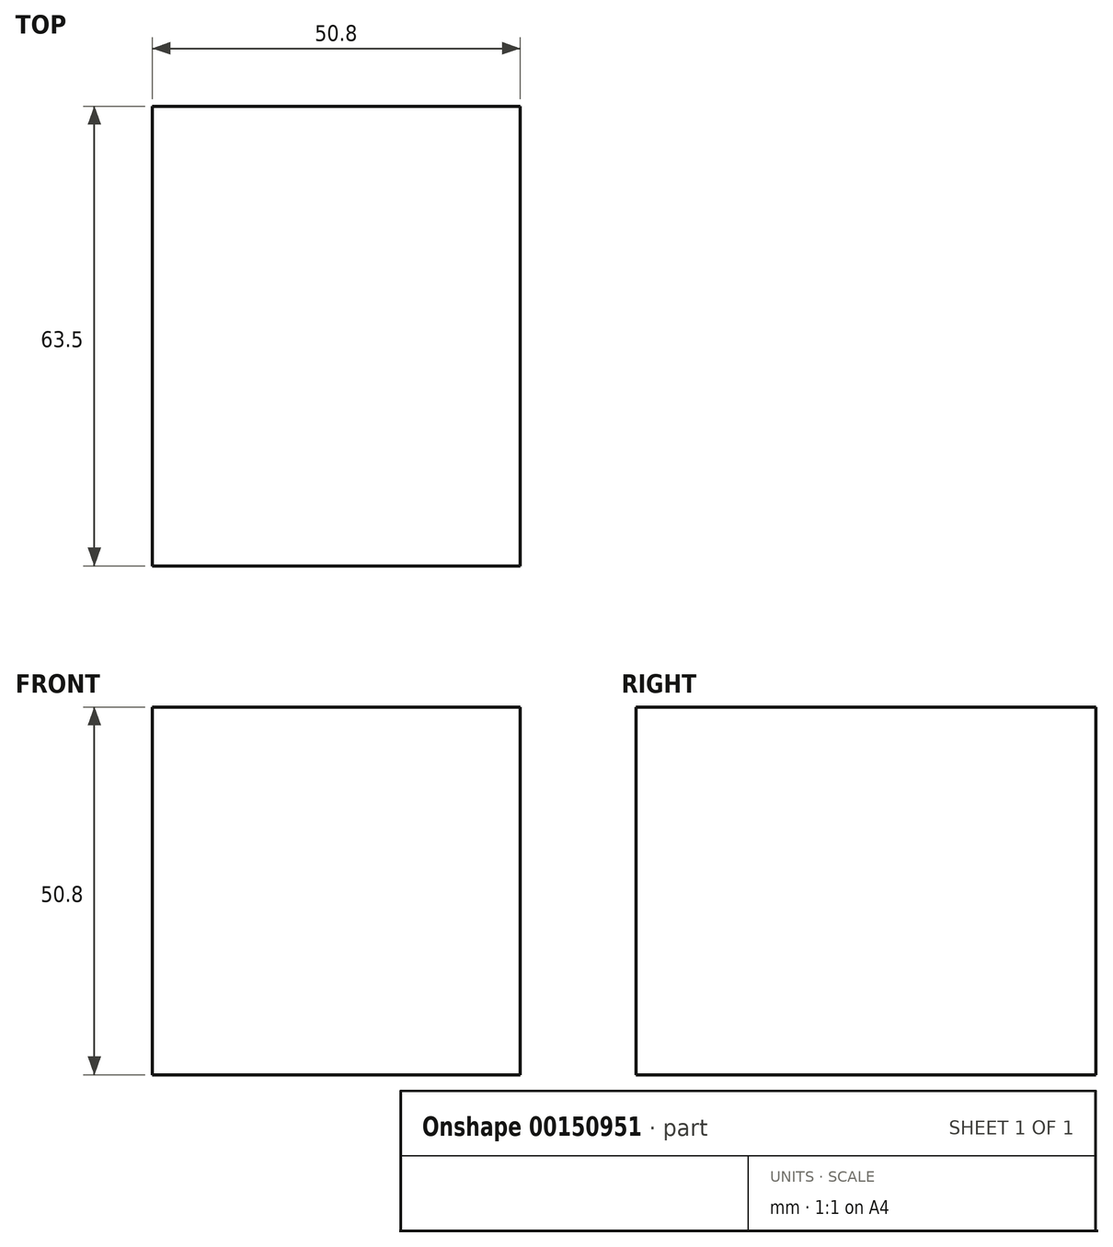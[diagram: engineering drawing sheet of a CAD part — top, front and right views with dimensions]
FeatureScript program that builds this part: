
annotation { "Feature Type Name" : "Feature", "Feature Type Description" : "" }
export const myFeature = defineFeature(function(context is Context, id is Id, definition is map)
    precondition{}
    {
        {
            var Q0;
            Q0=qCreatedBy(makeId("Front.planeOp"),FACE);
            var sketch = newSketch(context, id + "F0", { "sketchPlane" : qUnion([Q0])});
            skLineSegment(sketch, "E0.bottom", {"start": v(0, 0) * mm, "end": v(50.8, 0) * mm});
            skLineSegment(sketch, "E0.top", {"start": v(0, 50.8) * mm, "end": v(50.8, 50.8) * mm});
            skLineSegment(sketch, "E0.left", {"start": v(0, 0) * mm, "end": v(0, 50.8) * mm});
            skLineSegment(sketch, "E0.right", {"start": v(50.8, 0) * mm, "end": v(50.8, 50.8) * mm});
            skSolve(sketch);
        }
        {
            var Q0;
            Q0=makeQuery(id+"F0.imprint","IMPRINT",FACE,{"disambiguationData":[TD([[makeQuery(id+"F0.imprint","IMPRINT",EDGE,{"derivedFrom":sQuery(id+"F0.wireOp",EDGE,"E0.bottom")}),1.0]])]});
            extrude(context, id + "F1", {"entities" : qUnion([Q0]), "depth" : 63.5 * mm});
        }
    });
